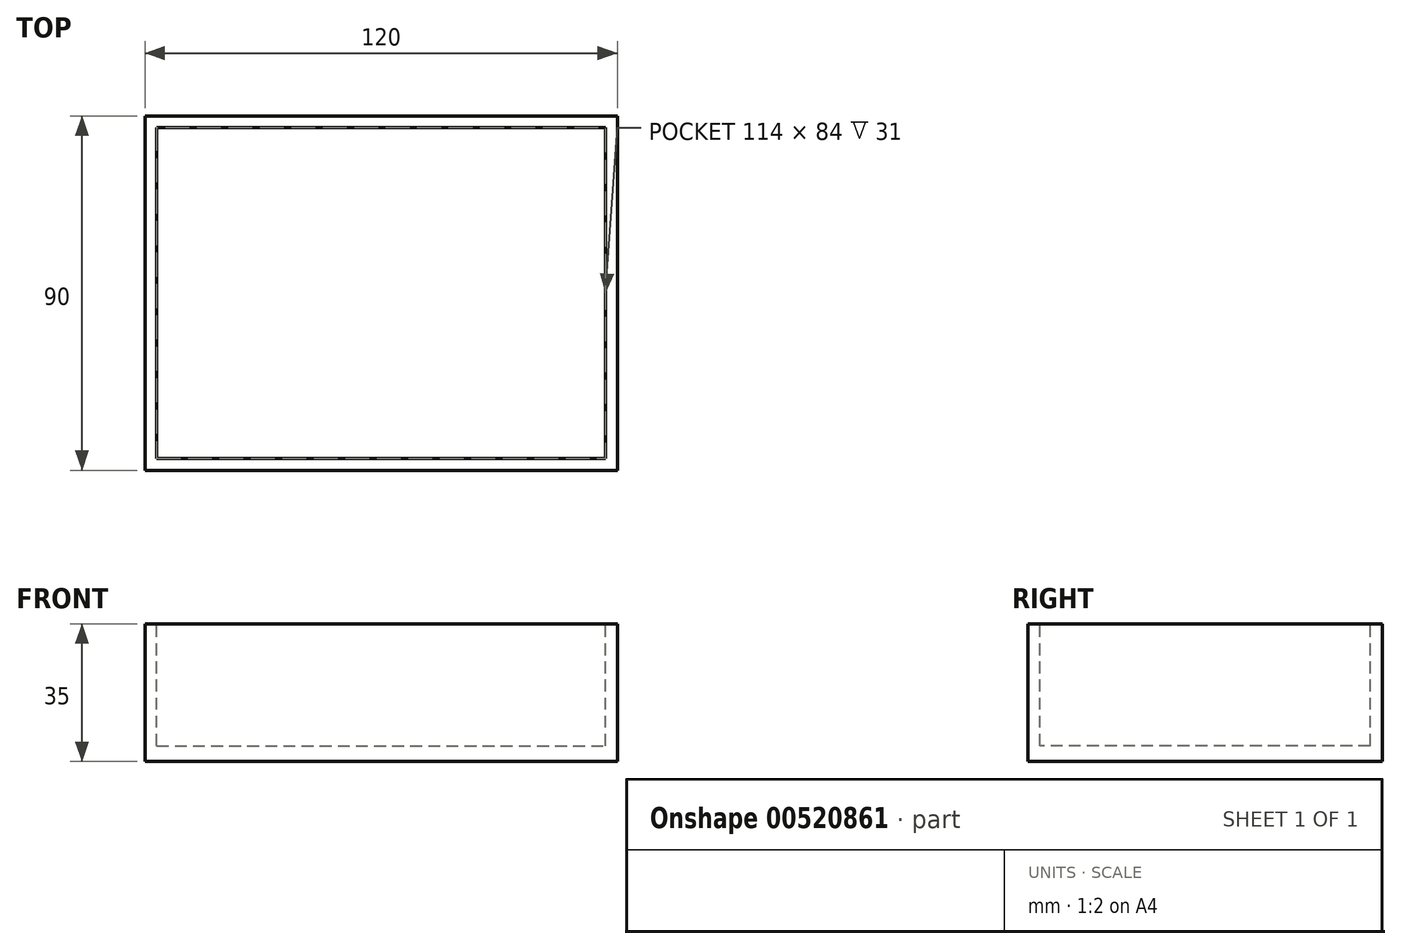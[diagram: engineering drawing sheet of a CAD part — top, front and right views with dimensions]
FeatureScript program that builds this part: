
annotation { "Feature Type Name" : "Feature", "Feature Type Description" : "" }
export const myFeature = defineFeature(function(context is Context, id is Id, definition is map)
    precondition{}
    {
        {
            var Q0;
            Q0=qCreatedBy(makeId("Top.planeOp"),FACE);
            var sketch = newSketch(context, id + "F0", { "sketchPlane" : qUnion([Q0])});
            skLineSegment(sketch, "E0.bottom", {"start": v(-60, 45) * mm, "end": v(60, 45) * mm});
            skLineSegment(sketch, "E0.top", {"start": v(-60, -45) * mm, "end": v(60, -45) * mm});
            skLineSegment(sketch, "E0.left", {"start": v(-60, 45) * mm, "end": v(-60, -45) * mm});
            skLineSegment(sketch, "E0.right", {"start": v(60, 45) * mm, "end": v(60, -45) * mm});
            skPoint(sketch, "E0.middle", {"position": v(0, 0) * mm});
            skSolve(sketch);
        }
        {
            var Q0;
            Q0=makeQuery(id+"F0.imprint","IMPRINT",FACE,{"disambiguationData":[TD([[makeQuery(id+"F0.imprint","IMPRINT",EDGE,{"derivedFrom":sQuery(id+"F0.wireOp",EDGE,"E0.bottom")}),-1.0]])]});
            extrude(context, id + "F1", {"entities" : qUnion([Q0]), "depth" : 35 * mm, "offsetDistance" : 25 * mm});
        }
        {
            var Q0;
            Q0=makeQuery(id+"F1.opExtrude","CAP_FACE",FACE,{"disambiguationData":[OSD([sQuery(id+"F0.wireOp",EDGE,"E0.bottom"),sQuery(id+"F0.wireOp",EDGE,"E0.top"),sQuery(id+"F0.wireOp",EDGE,"E0.left"),sQuery(id+"F0.wireOp",EDGE,"E0.right")])],"isStart":false});
            var sketch = newSketch(context, id + "F2", { "sketchPlane" : qUnion([Q0])});
            skLineSegment(sketch, "E1.bottom", {"start": v(-57, 42) * mm, "end": v(57, 42) * mm});
            skLineSegment(sketch, "E1.top", {"start": v(-57, -42) * mm, "end": v(57, -42) * mm});
            skLineSegment(sketch, "E1.left", {"start": v(-57, 42) * mm, "end": v(-57, -42) * mm});
            skLineSegment(sketch, "E1.right", {"start": v(57, 42) * mm, "end": v(57, -42) * mm});
            skPoint(sketch, "E1.middle", {"position": v(0, 0) * mm});
            skSolve(sketch);
        }
        {
            var Q0;
            Q0=makeQuery(id+"F2.imprint","IMPRINT",FACE,{"disambiguationData":[TD([[makeQuery(id+"F2.imprint","IMPRINT",EDGE,{"derivedFrom":sQuery(id+"F2.wireOp",EDGE,"E1.bottom")}),-1.0]])]});
            extrude(context, id + "F3", {"entities" : qUnion([Q0]), "operationType" : NewBodyOperationType.REMOVE, "oppositeDirection" : true, "depth" : 31 * mm, "offsetDistance" : 25 * mm});
        }
    });
